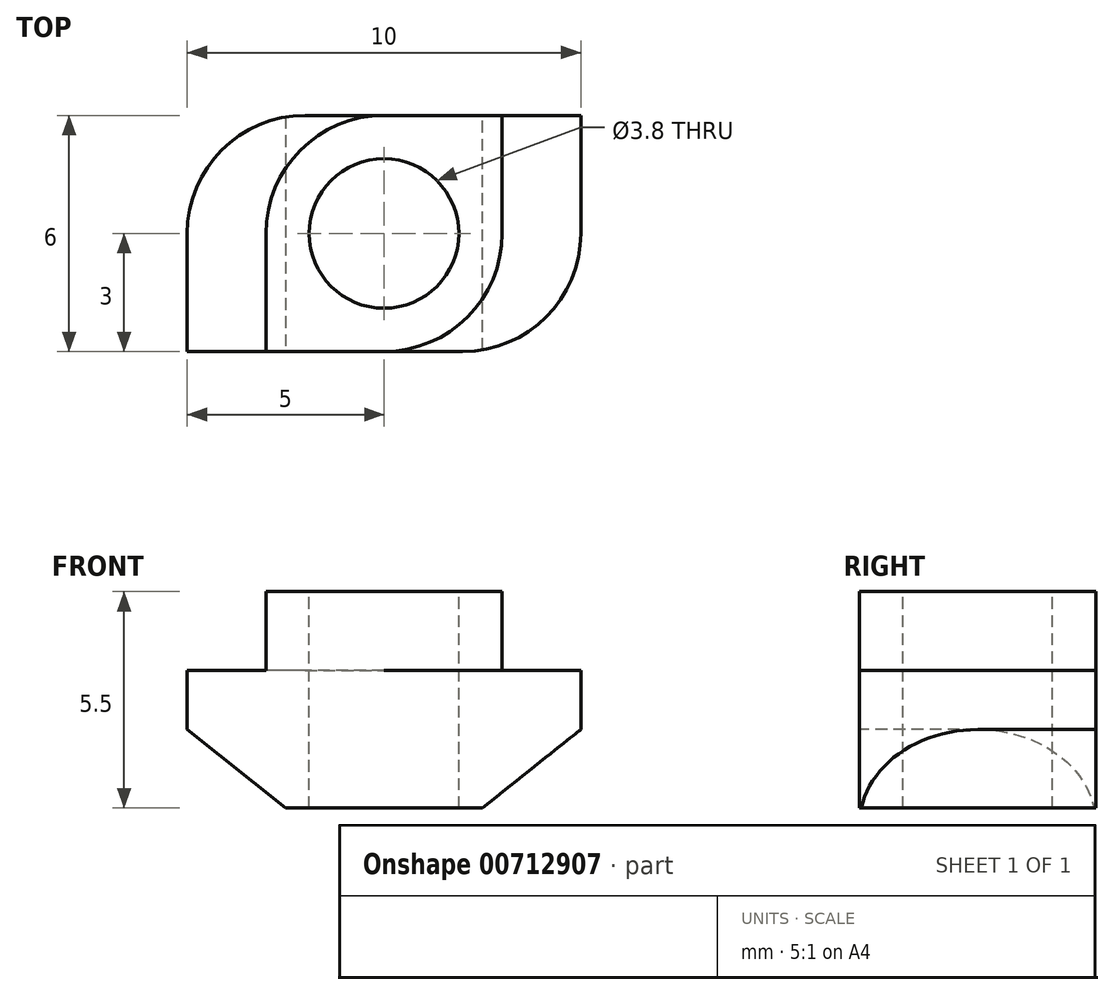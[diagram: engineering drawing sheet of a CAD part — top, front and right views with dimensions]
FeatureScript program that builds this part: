
annotation { "Feature Type Name" : "Feature", "Feature Type Description" : "" }
export const myFeature = defineFeature(function(context is Context, id is Id, definition is map)
    precondition{}
    {
        {
            var Q0;
            Q0=qCreatedBy(makeId("Top.planeOp"),FACE);
            var sketch = newSketch(context, id + "F0", { "sketchPlane" : qUnion([Q0])});
            skLineSegment(sketch, "E0.bottom", {"start": v(-5, -3) * mm, "end": v(2, -3) * mm});
            skLineSegment(sketch, "E0.top", {"start": v(-2, 3) * mm, "end": v(5, 3) * mm});
            skLineSegment(sketch, "E0.left", {"start": v(-5, -3) * mm, "end": v(-5, 0) * mm});
            skLineSegment(sketch, "E0.right", {"start": v(5, 0) * mm, "end": v(5, 3) * mm});
            skPoint(sketch, "E0.middle", {"position": v(0, 0) * mm});
            skArc(sketch, "E1", {"start": v(-2, 3) * mm, "mid": v(-4.12, 2.12) * mm, "end": v(-5, 0) * mm});
            skArc(sketch, "E2", {"start": v(2, -3) * mm, "mid": v(4.12, -2.12) * mm, "end": v(5, 0) * mm});
            skPoint(sketch, "E3.orphan", {"position": v(-5, 3) * mm});
            skPoint(sketch, "E4.orphan", {"position": v(5, -3) * mm});
            skSolve(sketch);
        }
        {
            var Q0;
            Q0=qSketchRegion(id+"F0",true);
            extrude(context, id + "F1", {"entities" : qUnion([Q0]), "depth" : 3.5 * mm, "offsetDistance" : 25 * mm});
        }
        {
            var Q0;
            Q0=makeQuery(id+"F1.opExtrude","CAP_FACE",FACE,{"disambiguationData":[OSD([sQuery(id+"F0.wireOp",EDGE,"E0.bottom"),sQuery(id+"F0.wireOp",EDGE,"E0.top"),sQuery(id+"F0.wireOp",EDGE,"E0.left"),sQuery(id+"F0.wireOp",EDGE,"E0.right"),sQuery(id+"F0.wireOp",EDGE,"E1"),sQuery(id+"F0.wireOp",EDGE,"E2")])],"isStart":false});
            var sketch = newSketch(context, id + "F2", { "sketchPlane" : qUnion([Q0])});
            skLineSegment(sketch, "E5.bottom", {"start": v(3, 3) * mm, "end": v(0, 3) * mm});
            skLineSegment(sketch, "E5.top", {"start": v(0, -3) * mm, "end": v(-3, -3) * mm});
            skLineSegment(sketch, "E5.left", {"start": v(3, 3) * mm, "end": v(3, 0) * mm});
            skLineSegment(sketch, "E5.right", {"start": v(-3, 0) * mm, "end": v(-3, -3) * mm});
            skPoint(sketch, "E5.middle", {"position": v(0, 0) * mm});
            skArc(sketch, "E6", {"start": v(0, -3) * mm, "mid": v(2.12, -2.12) * mm, "end": v(3, 0) * mm});
            skPoint(sketch, "E7.orphan", {"position": v(-3, 3) * mm});
            skPoint(sketch, "E8.orphan", {"position": v(3, -3) * mm});
            skArc(sketch, "E9.trimOffspring", {"start": v(0, 3) * mm, "mid": v(-2.12, 2.12) * mm, "end": v(-3, 0) * mm});
            skSolve(sketch);
        }
        {
            var Q0;
            Q0=makeQuery(id+"F2.imprint","IMPRINT",FACE,{"disambiguationData":[TD([[makeQuery(id+"F2.imprint","IMPRINT",EDGE,{"derivedFrom":sQuery(id+"F2.wireOp",EDGE,"E5.bottom")}),-1.0]])]});
            extrude(context, id + "F3", {"entities" : qUnion([Q0]), "operationType" : NewBodyOperationType.ADD, "depth" : 2 * mm, "offsetDistance" : 25 * mm});
        }
        {
            var Q0;
            Q0=makeQuery(id+"F3.opExtrude","CAP_FACE",FACE,{"disambiguationData":[OSD([sQuery(id+"F2.wireOp",EDGE,"E5.bottom"),sQuery(id+"F2.wireOp",EDGE,"E5.top"),sQuery(id+"F2.wireOp",EDGE,"E5.left"),sQuery(id+"F2.wireOp",EDGE,"E5.right"),sQuery(id+"F2.wireOp",EDGE,"E6"),sQuery(id+"F2.wireOp",EDGE,"E9.trimOffspring")])],"isStart":false});
            var sketch = newSketch(context, id + "F4", { "sketchPlane" : qUnion([Q0])});
            skCircle(sketch, "E10", {"center": v(0, 0) * mm, "radius": 1.9 * mm});
            skSolve(sketch);
        }
        {
            var Q0;
            Q0=qSketchRegion(id+"F4",true);
            extrude(context, id + "F5", {"entities" : qUnion([Q0]), "operationType" : NewBodyOperationType.REMOVE, "oppositeDirection" : true, "depth" : 25 * mm});
        }
        {
            var Q0;
            Q0=makeQuery(id+"F3.boolean.opBoolean","MERGE",FACE,{"derivedFrom":[makeQuery(id+"F1.opExtrude","SWEPT_FACE",FACE,{"disambiguationData":[OSD([sQuery(id+"F0.wireOp",EDGE,"E0.bottom")])]}),makeQuery(id+"F3.opExtrude","SWEPT_FACE",FACE,{"disambiguationData":[OSD([sQuery(id+"F2.wireOp",EDGE,"E5.top")])]})]});
            var sketch = newSketch(context, id + "F6", { "sketchPlane" : qUnion([Q0])});
            skLineSegment(sketch, "E11", {"start": v(-5, 2) * mm, "end": v(-2.5, 0) * mm});
            skLineSegment(sketch, "E12", {"start": v(-2.5, 0) * mm, "end": v(-5, 0) * mm});
            skLineSegment(sketch, "E13", {"start": v(-5, 0) * mm, "end": v(-5, 2) * mm});
            skSolve(sketch);
        }
        {
            var Q0;
            Q0=makeQuery(id+"F6.imprint","IMPRINT",FACE,{"disambiguationData":[TD([[makeQuery(id+"F6.imprint","IMPRINT",EDGE,{"derivedFrom":sQuery(id+"F6.wireOp",EDGE,"E11")}),-1.0]])]});
            extrude(context, id + "F7", {"entities" : qUnion([Q0]), "operationType" : NewBodyOperationType.REMOVE, "oppositeDirection" : true, "depth" : 25 * mm});
        }
        {
            var Q0;
            Q0=makeQuery(id+"F3.boolean.opBoolean","MERGE",FACE,{"derivedFrom":[makeQuery(id+"F1.opExtrude","SWEPT_FACE",FACE,{"disambiguationData":[OSD([sQuery(id+"F0.wireOp",EDGE,"E0.top")])]}),makeQuery(id+"F3.opExtrude","SWEPT_FACE",FACE,{"disambiguationData":[OSD([sQuery(id+"F2.wireOp",EDGE,"E5.bottom")])]})]});
            var sketch = newSketch(context, id + "F8", { "sketchPlane" : qUnion([Q0])});
            skLineSegment(sketch, "E14", {"start": v(-2.5, 0) * mm, "end": v(-5, 0) * mm});
            skLineSegment(sketch, "E15", {"start": v(-5, 0) * mm, "end": v(-5, 2) * mm});
            skLineSegment(sketch, "E16", {"start": v(-5, 2) * mm, "end": v(-2.5, 0) * mm});
            skSolve(sketch);
        }
        {
            var Q0;
            Q0=makeQuery(id+"F8.imprint","IMPRINT",FACE,{"disambiguationData":[TD([[makeQuery(id+"F8.imprint","IMPRINT",EDGE,{"derivedFrom":sQuery(id+"F8.wireOp",EDGE,"E14")}),-1.0]])]});
            extrude(context, id + "F9", {"entities" : qUnion([Q0]), "operationType" : NewBodyOperationType.REMOVE, "oppositeDirection" : true, "depth" : 25 * mm});
        }
    });
